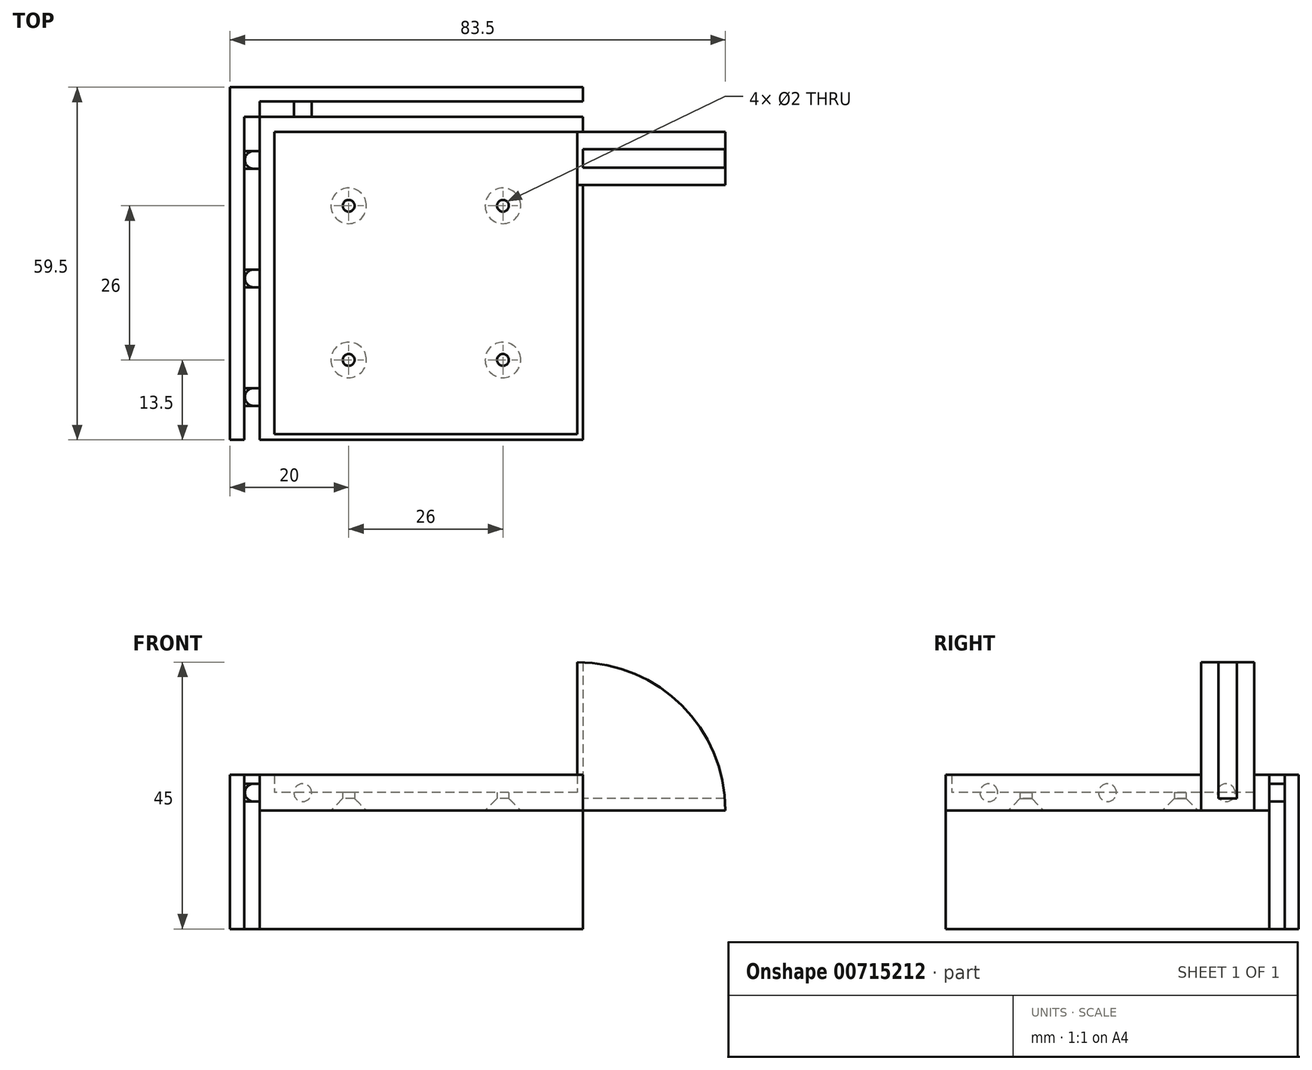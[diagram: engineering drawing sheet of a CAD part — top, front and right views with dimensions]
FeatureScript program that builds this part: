
annotation { "Feature Type Name" : "Feature", "Feature Type Description" : "" }
export const myFeature = defineFeature(function(context is Context, id is Id, definition is map)
    precondition{}
    {
        {
            var Q0;
            Q0=qCreatedBy(makeId("Top.planeOp"),FACE);
            var sketch = newSketch(context, id + "F0", { "sketchPlane" : qUnion([Q0])});
            skLineSegment(sketch, "E0.bottom", {"start": v(25.5, 25.5) * mm, "end": v(-25.5, 25.5) * mm});
            skLineSegment(sketch, "E0.top", {"start": v(25.5, -25.5) * mm, "end": v(-22.25, -25.5) * mm});
            skLineSegment(sketch, "E0.left", {"start": v(25.5, 25.5) * mm, "end": v(25.5, -25.5) * mm});
            skLineSegment(sketch, "E0.right", {"start": v(-25.5, 25.5) * mm, "end": v(-25.5, -25.5) * mm});
            skPoint(sketch, "E0.middle", {"position": v(0, 0) * mm});
            skLineSegment(sketch, "E1.0", {"start": v(28, 28) * mm, "end": v(-28, 28) * mm});
            skLineSegment(sketch, "E1.1", {"start": v(28, 28) * mm, "end": v(28, -28) * mm});
            skLineSegment(sketch, "E1.2", {"start": v(28, -28) * mm, "end": v(-22.25, -28) * mm});
            skLineSegment(sketch, "E1.3", {"start": v(-28, 28) * mm, "end": v(-28, -28) * mm});
            skCircle(sketch, "E2", {"center": v(-13, 13) * mm, "radius": 1 * mm});
            skLineSegment(sketch, "E3", {"start": v(0, 28) * mm, "end": v(0, -28) * mm, "construction": true});
            skLineSegment(sketch, "E4", {"start": v(-28, 0) * mm, "end": v(28, 0) * mm, "construction": true});
            skCircle(sketch, "E5.MirrorC", {"center": v(13, 13) * mm, "radius": 1 * mm});
            skCircle(sketch, "E6.MirrorC", {"center": v(13, -13) * mm, "radius": 1 * mm});
            skCircle(sketch, "E7.MirrorC", {"center": v(-13, -13) * mm, "radius": 1 * mm});
            skLineSegment(sketch, "E8.1", {"start": v(28, 33) * mm, "end": v(-33, 33) * mm});
            skLineSegment(sketch, "E9", {"start": v(28, 33) * mm, "end": v(28, 28) * mm});
            skLineSegment(sketch, "E10", {"start": v(-28, -28) * mm, "end": v(-33, -28) * mm});
            skLineSegment(sketch, "E11", {"start": v(28, 23.2) * mm, "end": v(28, 12.96) * mm});
            skLineSegment(sketch, "E12", {"start": v(28, 23.2) * mm, "end": v(28, 20) * mm});
            skLineSegment(sketch, "E13.trimOffspring", {"start": v(-25.25, -28) * mm, "end": v(-28, -28) * mm});
            skLineSegment(sketch, "E14", {"start": v(-25.5, -25.5) * mm, "end": v(-22.25, -25.5) * mm});
            skLineSegment(sketch, "E15", {"start": v(-25.25, -28) * mm, "end": v(-22.25, -28) * mm});
            skCircle(sketch, "E16", {"center": v(0, 0) * mm, "radius": 4.25 * mm});
            skLineSegment(sketch, "E17", {"start": v(-33, 33) * mm, "end": v(-33, -28) * mm});
            skSolve(sketch);
        }
        {
            var Q0;
            Q0=qCreatedBy(makeId("Top.planeOp"),FACE);
            var sketch = newSketch(context, id + "F1", { "sketchPlane" : qUnion([Q0])});
            skPoint(sketch, "E18.0", {"position": v(-25.5, -25.5) * mm});
            skLineSegment(sketch, "E19.bottom", {"start": v(-25.5, -25.5) * mm, "end": v(-16.5, -25.5) * mm});
            skLineSegment(sketch, "E19.top", {"start": v(-25.5, -50.5) * mm, "end": v(-16.5, -50.5) * mm});
            skLineSegment(sketch, "E19.left", {"start": v(-25.5, -25.5) * mm, "end": v(-25.5, -50.5) * mm});
            skLineSegment(sketch, "E19.right", {"start": v(-16.5, -25.5) * mm, "end": v(-16.5, -50.5) * mm});
            skLineSegment(sketch, "E20", {"start": v(-21, -50.5) * mm, "end": v(-21, -25.5) * mm, "construction": true});
            skLineSegment(sketch, "E21", {"start": v(-19.45, -25.5) * mm, "end": v(-19.45, -50.5) * mm});
            skLineSegment(sketch, "E22.MirrorCS", {"start": v(-22.55, -25.5) * mm, "end": v(-22.55, -50.5) * mm});
            skPoint(sketch, "E23.0", {"position": v(25.5, 25.5) * mm});
            skLineSegment(sketch, "E24.bottom", {"start": v(25.5, 25.5) * mm, "end": v(50.5, 25.5) * mm});
            skLineSegment(sketch, "E24.top", {"start": v(25.5, 16.5) * mm, "end": v(50.5, 16.5) * mm});
            skLineSegment(sketch, "E24.left", {"start": v(25.5, 25.5) * mm, "end": v(25.5, 16.5) * mm});
            skLineSegment(sketch, "E24.right", {"start": v(50.5, 25.5) * mm, "end": v(50.5, 16.5) * mm});
            skLineSegment(sketch, "E25", {"start": v(25.5, 21) * mm, "end": v(50.5, 21) * mm, "construction": true});
            skLineSegment(sketch, "E26", {"start": v(50.5, 22.55) * mm, "end": v(25.5, 22.55) * mm});
            skLineSegment(sketch, "E27.MirrorCS", {"start": v(50.5, 19.45) * mm, "end": v(25.5, 19.45) * mm});
            skSolve(sketch);
        }
        {
            var Q0;
            Q0=makeQuery(id+"F0.imprint","IMPRINT",FACE,{"disambiguationData":[TD([[makeQuery(id+"F0.imprint","IMPRINT",EDGE,{"derivedFrom":sQuery(id+"F0.wireOp",EDGE,"E0.bottom")}),1.0]])]});
            var Q1;
            Q1=makeQuery(id+"F0.imprint","IMPRINT",FACE,{"disambiguationData":[TD([[makeQuery(id+"F0.imprint","IMPRINT",EDGE,{"derivedFrom":sQuery(id+"F0.wireOp",EDGE,"E16")}),1.0]])]});
            extrude(context, id + "F2", {"entities" : qUnion([Q0, Q1]), "depth" : 3 * mm, "offsetDistance" : 25 * mm});
        }
        {
            var Q0;
            Q0=makeQuery(id+"F0.imprint","IMPRINT",FACE,{"disambiguationData":[TD([[makeQuery(id+"F0.imprint","IMPRINT",EDGE,{"derivedFrom":sQuery(id+"F0.wireOp",EDGE,"E0.bottom")}),-1.0]])]});
            var Q1;
            {var subQ5=sQuery(id+"F0.wireOp",EDGE,"TI18WCdd-EPFC-hNpH-Rctt-afuqL8Zf6Xfq");Q1=makeQuery(id+"F0.imprint","IMPRINT",FACE,{"disambiguationData":[TD([[makeQuery(id+"F0.imprint","IMPRINT",EDGE,{"derivedFrom":subQ5}),-1.0]])]});}
            extrude(context, id + "F3", {"entities" : qUnion([Q0, Q1]), "operationType" : NewBodyOperationType.ADD, "depth" : 6 * mm, "offsetDistance" : 25 * mm});
        }
        {
            var Q0;
            Q0=makeQuery(id+"F2.opExtrude","CAP_EDGE",EDGE,{"disambiguationData":[OSD([sQuery(id+"F0.wireOp",EDGE,"E7.MirrorC")])],"isStart":true});
            var Q1;
            Q1=makeQuery(id+"F2.opExtrude","CAP_EDGE",EDGE,{"disambiguationData":[OSD([sQuery(id+"F0.wireOp",EDGE,"E6.MirrorC")])],"isStart":true});
            var Q2;
            Q2=makeQuery(id+"F2.opExtrude","CAP_EDGE",EDGE,{"disambiguationData":[OSD([sQuery(id+"F0.wireOp",EDGE,"E5.MirrorC")])],"isStart":true});
            var Q3;
            Q3=makeQuery(id+"F2.opExtrude","CAP_EDGE",EDGE,{"disambiguationData":[OSD([sQuery(id+"F0.wireOp",EDGE,"E2")])],"isStart":true});
            chamfer(context, id + "F4", {"entities" : qUnion([Q0, Q1, Q2, Q3]), "width" : 2 * mm, "tangentPropagation" : true});
        }
        {
            var Q0;
            Q0=makeQuery(id+"FIbiUBh41szAzK7_1.boolean.opBoolean","MERGE",FACE,{"derivedFrom":[makeQuery(id+"F3.opExtrude","SWEPT_FACE",FACE,{"disambiguationData":[OSD([sQuery(id+"F0.wireOp",EDGE,"E1.2"),sQuery(id+"F0.wireOp",EDGE,"E13.trimOffspring"),sQuery(id+"F0.wireOp",EDGE,"E15")])]}),makeQuery(id+"FIbiUBh41szAzK7_1.opExtrude","SWEPT_FACE",FACE,{"disambiguationData":[OSD([sQuery(id+"F0.wireOp",EDGE,"E10")])]})]});
            extrude(context, id + "F5", {"entities" : qUnion([Q0]), "operationType" : NewBodyOperationType.REMOVE, "oppositeDirection" : true, "depth" : 1.5 * mm, "offsetDistance" : 25 * mm});
        }
        {
            var Q0;
            Q0=makeQuery(id+"FIbiUBh41szAzK7_1.boolean.opBoolean","MERGE",FACE,{"derivedFrom":[makeQuery(id+"F3.opExtrude","SWEPT_FACE",FACE,{"disambiguationData":[OSD([sQuery(id+"F0.wireOp",EDGE,"E1.1"),sQuery(id+"F0.wireOp",EDGE,"E11"),sQuery(id+"F0.wireOp",EDGE,"E12")])]}),makeQuery(id+"FIbiUBh41szAzK7_1.opExtrude","SWEPT_FACE",FACE,{"disambiguationData":[OSD([sQuery(id+"F0.wireOp",EDGE,"E9")])]})]});
            extrude(context, id + "F6", {"entities" : qUnion([Q0]), "operationType" : NewBodyOperationType.REMOVE, "oppositeDirection" : true, "depth" : 1.5 * mm, "offsetDistance" : 25 * mm});
        }
        {
            var Q0;
            {var subQ0=sQuery(id+"F1.wireOp",EDGE,"E24.top");Q0=makeQuery(id+"F1.imprint","IMPRINT",FACE,{"disambiguationData":[TD([[makeQuery(id+"F1.imprint","IMPRINT",EDGE,{"derivedFrom":subQ0}),1.0]])]});}
            var Q1;
            {var subQ0=sQuery(id+"F1.wireOp",EDGE,"E24.bottom");Q1=makeQuery(id+"F1.imprint","IMPRINT",FACE,{"disambiguationData":[TD([[makeQuery(id+"F1.imprint","IMPRINT",EDGE,{"derivedFrom":subQ0}),-1.0]])]});}
            extrude(context, id + "F7", {"entities" : qUnion([Q0, Q1]), "operationType" : NewBodyOperationType.ADD, "depth" : 25 * mm, "offsetDistance" : 25 * mm});
        }
        {
            var Q0;
            {var subQ0=sQuery(id+"F1.wireOp",EDGE,"E26");Q0=makeQuery(id+"F1.imprint","IMPRINT",FACE,{"disambiguationData":[TD([[makeQuery(id+"F1.imprint","IMPRINT",EDGE,{"derivedFrom":subQ0}),1.0]])]});}
            extrude(context, id + "F8", {"entities" : qUnion([Q0]), "operationType" : NewBodyOperationType.ADD, "depth" : 2 * mm, "offsetDistance" : 25 * mm});
        }
        {
            var Q0;
            {var subQ1=sQuery(id+"F1.wireOp",EDGE,"E26");var subQ2=sQuery(id+"F0.wireOp",EDGE,"E12");var subQ3=sQuery(id+"F0.wireOp",EDGE,"E11");var subQ4=sQuery(id+"F0.wireOp",EDGE,"E1.1");var subQ6=sQuery(id+"F0.wireOp",EDGE,"E0.left");Q0=makeQuery(id+"F7.boolean.opBoolean","SPLIT",FACE,{"disambiguationData":[TD([makeQuery(id+"F7.opExtrude","SWEPT_FACE",FACE,{"disambiguationData":[OSD([subQ1])]})])],"derivedFrom":makeQuery(id+"F3.opExtrude","CAP_FACE",FACE,{"disambiguationData":[OSD([sQuery(id+"F0.wireOp",EDGE,"E0.bottom"),sQuery(id+"F0.wireOp",EDGE,"E0.top"),subQ6,sQuery(id+"F0.wireOp",EDGE,"E0.right"),sQuery(id+"F0.wireOp",EDGE,"E1.0"),subQ4,sQuery(id+"F0.wireOp",EDGE,"E1.2"),sQuery(id+"F0.wireOp",EDGE,"E1.3"),subQ3,subQ2,sQuery(id+"F0.wireOp",EDGE,"E13.trimOffspring"),sQuery(id+"F0.wireOp",EDGE,"E14"),sQuery(id+"F0.wireOp",EDGE,"E15")])],"isStart":false})});}
            var Q1;
            Q1=makeQuery(id+"F7.opExtrude","CAP_FACE",FACE,{"disambiguationData":[OSD([sQuery(id+"F1.wireOp",EDGE,"E24.bottom"),sQuery(id+"F1.wireOp",EDGE,"E24.left"),sQuery(id+"F1.wireOp",EDGE,"E24.right"),sQuery(id+"F1.wireOp",EDGE,"E26")])],"isStart":false});
            var Q2;
            Q2=makeQuery(id+"F2.opExtrude","SWEPT_BODY",BODY,{"disambiguationData":[OSD([sQuery(id+"F0.wireOp",EDGE,"E0.bottom"),sQuery(id+"F0.wireOp",EDGE,"E0.top"),sQuery(id+"F0.wireOp",EDGE,"E0.left"),sQuery(id+"F0.wireOp",EDGE,"E0.right"),sQuery(id+"F0.wireOp",EDGE,"E2"),sQuery(id+"F0.wireOp",EDGE,"E5.MirrorC"),sQuery(id+"F0.wireOp",EDGE,"E6.MirrorC"),sQuery(id+"F0.wireOp",EDGE,"E7.MirrorC"),sQuery(id+"F0.wireOp",EDGE,"E14"),sQuery(id+"F0.wireOp",EDGE,"E16")])]});
            extrude(context, id + "F9", {"entities" : qUnion([Q0]), "operationType" : NewBodyOperationType.ADD, "endBound" : BoundingType.UP_TO_SURFACE, "depth" : 25 * mm, "endBoundEntityFace" : qUnion([Q1]), "endBoundEntityBody" : qUnion([Q2]), "offsetDistance" : 25 * mm});
        }
        {
            var Q0;
            {var subQ0=sQuery(id+"F1.wireOp",EDGE,"E19.top");Q0=makeQuery(id+"F7.opExtrude","CAP_EDGE",EDGE,{"disambiguationData":[OSD([subQ0]),TDD([makeQuery(id+"F1.imprint","IMPRINT",EDGE,{"disambiguationData":[TD([[makeQuery(id+"F1.imprint","INTERSECT",VERTEX,{"derivedFrom":[subQ0,sQuery(id+"F1.wireOp",EDGE,"E19.left")]}),-1.0]])],"derivedFrom":subQ0})])],"isStart":false});}
            var Q1;
            {var subQ0=sQuery(id+"F1.wireOp",EDGE,"E19.top");Q1=makeQuery(id+"F7.opExtrude","CAP_EDGE",EDGE,{"disambiguationData":[OSD([subQ0]),TDD([makeQuery(id+"F1.imprint","IMPRINT",EDGE,{"disambiguationData":[TD([[makeQuery(id+"F1.imprint","INTERSECT",VERTEX,{"derivedFrom":[subQ0,sQuery(id+"F1.wireOp",EDGE,"E19.right")]}),1.0]])],"derivedFrom":subQ0})])],"isStart":false});}
            var Q2;
            {var subQ0=sQuery(id+"F1.wireOp",EDGE,"E24.right");Q2=makeQuery(id+"F7.opExtrude","CAP_EDGE",EDGE,{"disambiguationData":[OSD([subQ0]),TDD([makeQuery(id+"F1.imprint","IMPRINT",EDGE,{"disambiguationData":[TD([[makeQuery(id+"F1.imprint","INTERSECT",VERTEX,{"derivedFrom":[sQuery(id+"F1.wireOp",EDGE,"E24.bottom"),subQ0]}),-1.0]])],"derivedFrom":subQ0})])],"isStart":false});}
            fillet(context, id + "F10", {"entities" : qUnion([Q0, Q1, Q2]), "radius" : 25 * mm, "tangentPropagation" : true, "allowEdgeOverflow" : false});
        }
        {
            var Q0;
            Q0=makeQuery(id+"F3.opExtrude","SWEPT_FACE",FACE,{"disambiguationData":[OSD([sQuery(id+"F0.wireOp",EDGE,"E1.3")])]});
            var sketch = newSketch(context, id + "F11", { "sketchPlane" : qUnion([Q0])});
            skCircle(sketch, "E28", {"center": v(-20.75, 3) * mm, "radius": 1.5 * mm});
            skPoint(sketch, "E28.centerSnap0", {"position": v(-28, 3) * mm});
            skCircle(sketch, "E29", {"center": v(19.25, 3) * mm, "radius": 1.5 * mm});
            skCircle(sketch, "E30", {"center": v(-0.75, 3) * mm, "radius": 1.5 * mm});
            skPoint(sketch, "E30.centerSnap0", {"position": v(-0.75, 6) * mm});
            skSolve(sketch);
        }
        {
            var Q0;
            Q0=makeQuery(id+"F11.imprint","IMPRINT",FACE,{"disambiguationData":[TD([[makeQuery(id+"F11.imprint","IMPRINT",EDGE,{"derivedFrom":sQuery(id+"F11.wireOp",EDGE,"E28")}),1.0]])]});
            var Q1;
            Q1=makeQuery(id+"F11.imprint","IMPRINT",FACE,{"disambiguationData":[TD([[makeQuery(id+"F11.imprint","IMPRINT",EDGE,{"derivedFrom":sQuery(id+"F11.wireOp",EDGE,"E30")}),1.0]])]});
            var Q2;
            Q2=makeQuery(id+"F11.imprint","IMPRINT",FACE,{"disambiguationData":[TD([[makeQuery(id+"F11.imprint","IMPRINT",EDGE,{"derivedFrom":sQuery(id+"F11.wireOp",EDGE,"E29")}),1.0]])]});
            extrude(context, id + "F12", {"entities" : qUnion([Q0, Q1, Q2]), "operationType" : NewBodyOperationType.ADD, "depth" : 2.5 * mm, "offsetDistance" : 25 * mm});
        }
        {
            var Q0;
            Q0=makeQuery(id+"F3.opExtrude","SWEPT_FACE",FACE,{"disambiguationData":[OSD([sQuery(id+"F0.wireOp",EDGE,"E1.0")])]});
            var sketch = newSketch(context, id + "F13", { "sketchPlane" : qUnion([Q0])});
            skCircle(sketch, "E31", {"center": v(0.75, 3) * mm, "radius": 1.5 * mm});
            skPoint(sketch, "E31.centerSnap0", {"position": v(28, 3) * mm});
            skPoint(sketch, "E31.centerSnap1", {"position": v(0.75, 6) * mm});
            skCircle(sketch, "E32", {"center": v(20.75, 3) * mm, "radius": 1.5 * mm});
            skCircle(sketch, "E33", {"center": v(-19.25, 3) * mm, "radius": 1.5 * mm});
            skSolve(sketch);
        }
        {
            var Q0;
            Q0=makeQuery(id+"F13.imprint","IMPRINT",FACE,{"disambiguationData":[TD([[makeQuery(id+"F13.imprint","IMPRINT",EDGE,{"derivedFrom":sQuery(id+"F13.wireOp",EDGE,"E33")}),1.0]])]});
            var Q1;
            Q1=makeQuery(id+"F13.imprint","IMPRINT",FACE,{"disambiguationData":[TD([[makeQuery(id+"F13.imprint","IMPRINT",EDGE,{"derivedFrom":sQuery(id+"F13.wireOp",EDGE,"E31")}),1.0]])]});
            extrude(context, id + "F14", {"entities" : qUnion([Q0, Q1]), "operationType" : NewBodyOperationType.ADD, "depth" : 2.5 * mm, "offsetDistance" : 25 * mm});
        }
        {
            var Q0;
            Q0=makeQuery(id+"F12.opExtrude","CAP_FACE",FACE,{"disambiguationData":[OSD([sQuery(id+"F11.wireOp",EDGE,"E28")])],"isStart":false});
            var Q1;
            Q1=makeQuery(id+"F12.opExtrude","CAP_FACE",FACE,{"disambiguationData":[OSD([sQuery(id+"F11.wireOp",EDGE,"E30")])],"isStart":false});
            var Q2;
            Q2=makeQuery(id+"F12.opExtrude","CAP_FACE",FACE,{"disambiguationData":[OSD([sQuery(id+"F11.wireOp",EDGE,"E29")])],"isStart":false});
            var Q3;
            Q3=makeQuery(id+"F14.opExtrude","CAP_FACE",FACE,{"disambiguationData":[OSD([sQuery(id+"F13.wireOp",EDGE,"E33")])],"isStart":false});
            var Q4;
            Q4=makeQuery(id+"F14.opExtrude","CAP_FACE",FACE,{"disambiguationData":[OSD([sQuery(id+"F13.wireOp",EDGE,"E31")])],"isStart":false});
            fillet(context, id + "F15", {"entities" : qUnion([Q0, Q1, Q2, Q3, Q4]), "radius" : 1.5 * mm, "tangentPropagation" : true, "allowEdgeOverflow" : false});
        }
        {
            var Q0;
            Q0=makeQuery(id+"F0.imprint","IMPRINT",FACE,{"disambiguationData":[TD([[makeQuery(id+"F0.imprint","IMPRINT",EDGE,{"derivedFrom":sQuery(id+"F0.wireOp",EDGE,"E1.0")}),-1.0]])]});
            extrude(context, id + "F16", {"entities" : qUnion([Q0]), "depth" : 6 * mm, "offsetDistance" : 25 * mm, "hasSecondDirection" : true, "secondDirectionOppositeDirection" : true, "secondDirectionDepth" : 20 * mm});
        }
        {
            var Q0;
            Q0=makeQuery(id+"F16.opExtrude","SWEPT_FACE",FACE,{"disambiguationData":[OSD([sQuery(id+"F0.wireOp",EDGE,"E9")])]});
            extrude(context, id + "F17", {"entities" : qUnion([Q0]), "operationType" : NewBodyOperationType.REMOVE, "oppositeDirection" : true, "depth" : 1.5 * mm, "offsetDistance" : 25 * mm});
        }
        {
            var Q0;
            Q0=makeQuery(id+"F16.opExtrude","SWEPT_FACE",FACE,{"disambiguationData":[OSD([sQuery(id+"F0.wireOp",EDGE,"E10")])]});
            extrude(context, id + "F18", {"entities" : qUnion([Q0]), "operationType" : NewBodyOperationType.REMOVE, "oppositeDirection" : true, "depth" : 1.5 * mm, "offsetDistance" : 25 * mm});
        }
        {
            var Q0;
            Q0=makeQuery(id+"F16.opExtrude","SWEPT_FACE",FACE,{"disambiguationData":[OSD([sQuery(id+"F0.wireOp",EDGE,"E1.3")])]});
            var sketch = newSketch(context, id + "F19", { "sketchPlane" : qUnion([Q0])});
            skCircle(sketch, "E34.0", {"center": v(20.75, 3) * mm, "radius": 1.5 * mm});
            skCircle(sketch, "E34.1", {"center": v(0.75, 3) * mm, "radius": 1.5 * mm});
            skCircle(sketch, "E34.2", {"center": v(-19.25, 3) * mm, "radius": 1.5 * mm});
            skSolve(sketch);
        }
        {
            var Q0;
            Q0=makeQuery(id+"F16.opExtrude","SWEPT_FACE",FACE,{"disambiguationData":[OSD([sQuery(id+"F0.wireOp",EDGE,"E1.0")])]});
            var sketch = newSketch(context, id + "F20", { "sketchPlane" : qUnion([Q0])});
            skCircle(sketch, "E35.0", {"center": v(-20.75, 3) * mm, "radius": 1.5 * mm});
            skCircle(sketch, "E35.1", {"center": v(-0.75, 3) * mm, "radius": 1.5 * mm});
            skCircle(sketch, "E35.2", {"center": v(19.25, 3) * mm, "radius": 1.5 * mm});
            skSolve(sketch);
        }
        {
            var Q0;
            Q0=makeQuery(id+"F20.imprint","IMPRINT",FACE,{"disambiguationData":[TD([[makeQuery(id+"F20.imprint","IMPRINT",EDGE,{"derivedFrom":sQuery(id+"F20.wireOp",EDGE,"E35.0")}),-1.0]])]});
            var Q1;
            Q1=makeQuery(id+"F13.imprint","IMPRINT",FACE,{"disambiguationData":[TD([[makeQuery(id+"F13.imprint","IMPRINT",EDGE,{"derivedFrom":sQuery(id+"F13.wireOp",EDGE,"E31")}),1.0]])]});
            var Q2;
            Q2=makeQuery(id+"F13.imprint","IMPRINT",FACE,{"disambiguationData":[TD([[makeQuery(id+"F13.imprint","IMPRINT",EDGE,{"derivedFrom":sQuery(id+"F13.wireOp",EDGE,"E33")}),1.0]])]});
            extrude(context, id + "F21", {"entities" : qUnion([Q0, Q1, Q2]), "operationType" : NewBodyOperationType.REMOVE, "oppositeDirection" : true, "depth" : 2.6 * mm, "offsetDistance" : 25 * mm});
        }
        {
            var Q0;
            Q0=makeQuery(id+"F19.imprint","IMPRINT",FACE,{"disambiguationData":[TD([[makeQuery(id+"F19.imprint","IMPRINT",EDGE,{"derivedFrom":sQuery(id+"F19.wireOp",EDGE,"E34.0")}),-1.0]])]});
            var Q1;
            Q1=makeQuery(id+"F19.imprint","IMPRINT",FACE,{"disambiguationData":[TD([[makeQuery(id+"F19.imprint","IMPRINT",EDGE,{"derivedFrom":sQuery(id+"F19.wireOp",EDGE,"E34.1")}),-1.0]])]});
            var Q2;
            Q2=makeQuery(id+"F19.imprint","IMPRINT",FACE,{"disambiguationData":[TD([[makeQuery(id+"F19.imprint","IMPRINT",EDGE,{"derivedFrom":sQuery(id+"F19.wireOp",EDGE,"E34.2")}),-1.0]])]});
            extrude(context, id + "F22", {"entities" : qUnion([Q0, Q1, Q2]), "operationType" : NewBodyOperationType.REMOVE, "oppositeDirection" : true, "depth" : 2.6 * mm, "offsetDistance" : 25 * mm});
        }
    });
